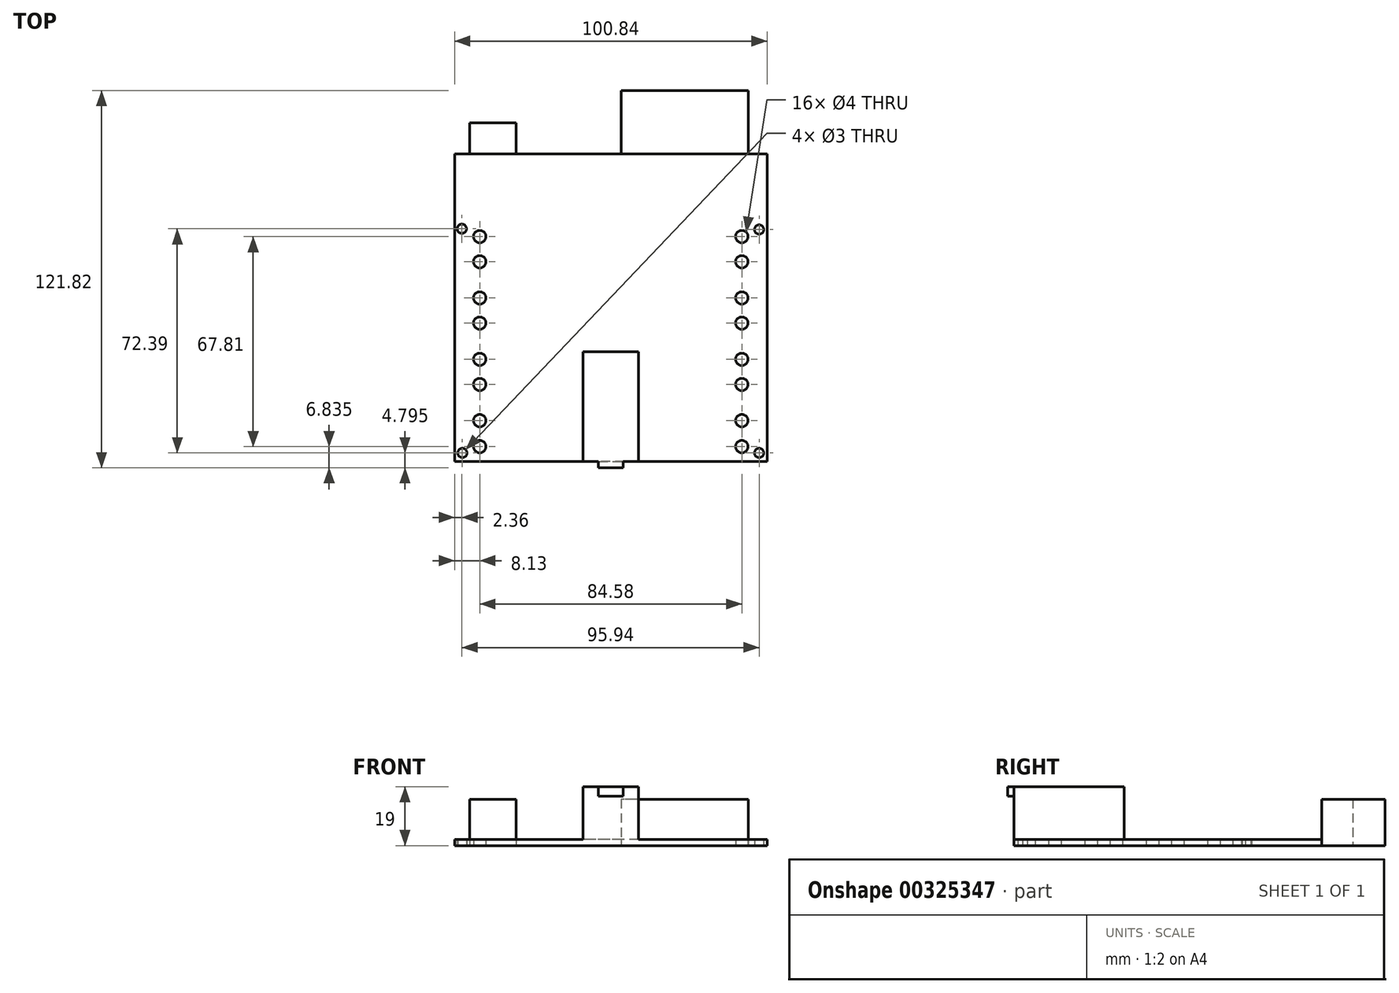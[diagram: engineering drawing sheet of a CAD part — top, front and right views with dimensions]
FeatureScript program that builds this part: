
annotation { "Feature Type Name" : "Feature", "Feature Type Description" : "" }
export const myFeature = defineFeature(function(context is Context, id is Id, definition is map)
    precondition{}
    {
        {
            var Q0;
            Q0=qCreatedBy(makeId("Top.planeOp"),FACE);
            var sketch = newSketch(context, id + "F0", { "sketchPlane" : qUnion([Q0])});
            skLineSegment(sketch, "E0.bottom", {"start": v(50.42, -49.66) * mm, "end": v(-50.42, -49.66) * mm});
            skLineSegment(sketch, "E0.top", {"start": v(50.42, 49.66) * mm, "end": v(-50.42, 49.66) * mm});
            skLineSegment(sketch, "E0.left", {"start": v(50.42, -49.66) * mm, "end": v(50.42, 49.66) * mm});
            skLineSegment(sketch, "E0.right", {"start": v(-50.42, -49.66) * mm, "end": v(-50.42, 49.66) * mm});
            skPoint(sketch, "E0.middle", {"position": v(0, 0) * mm});
            skCircle(sketch, "E1", {"center": v(-48.06, 25.53) * mm, "radius": 1.5 * mm});
            skCircle(sketch, "E2", {"center": v(47.88, -46.86) * mm, "radius": 1.5 * mm});
            skCircle(sketch, "E3", {"center": v(47.88, 25.28) * mm, "radius": 1.5 * mm});
            skCircle(sketch, "E4", {"center": v(-47.88, -46.87) * mm, "radius": 1.5 * mm});
            skCircle(sketch, "E5", {"center": v(-42.29, -44.83) * mm, "radius": 2 * mm});
            skCircle(sketch, "E6", {"center": v(-42.29, -36.45) * mm, "radius": 2 * mm});
            skCircle(sketch, "E7", {"center": v(-42.29, -24.77) * mm, "radius": 2 * mm});
            skCircle(sketch, "E8", {"center": v(-42.29, -16.64) * mm, "radius": 2 * mm});
            skCircle(sketch, "E9", {"center": v(-42.29, -4.96) * mm, "radius": 2 * mm});
            skCircle(sketch, "E10", {"center": v(-42.29, 3.17) * mm, "radius": 2 * mm});
            skCircle(sketch, "E11", {"center": v(-42.29, 14.85) * mm, "radius": 2 * mm});
            skCircle(sketch, "E12", {"center": v(-42.29, 22.98) * mm, "radius": 2 * mm});
            skCircle(sketch, "E13", {"center": v(42.3, -44.83) * mm, "radius": 2 * mm});
            skCircle(sketch, "E14", {"center": v(42.3, -36.45) * mm, "radius": 2 * mm});
            skCircle(sketch, "E15", {"center": v(42.29, -24.77) * mm, "radius": 2 * mm});
            skCircle(sketch, "E16", {"center": v(42.29, -16.64) * mm, "radius": 2 * mm});
            skCircle(sketch, "E17", {"center": v(42.29, -4.96) * mm, "radius": 2 * mm});
            skCircle(sketch, "E18", {"center": v(42.29, 3.17) * mm, "radius": 2 * mm});
            skCircle(sketch, "E19", {"center": v(42.29, 14.85) * mm, "radius": 2 * mm});
            skCircle(sketch, "E20", {"center": v(42.29, 22.98) * mm, "radius": 2 * mm});
            skSolve(sketch);
        }
        {
            var Q0;
            Q0=qSketchRegion(id+"F0",true);
            extrude(context, id + "F1", {"entities" : qUnion([Q0]), "depth" : 2 * mm});
        }
        {
            var Q0;
            Q0=makeQuery(id+"F1.opExtrude","CAP_FACE",FACE,{"disambiguationData":[OSD([sQuery(id+"F0.wireOp",EDGE,"E0.bottom"),sQuery(id+"F0.wireOp",EDGE,"E0.top"),sQuery(id+"F0.wireOp",EDGE,"E0.left"),sQuery(id+"F0.wireOp",EDGE,"E0.right"),sQuery(id+"F0.wireOp",EDGE,"E1"),sQuery(id+"F0.wireOp",EDGE,"E2"),sQuery(id+"F0.wireOp",EDGE,"E3"),sQuery(id+"F0.wireOp",EDGE,"E4")])],"isStart":false});
            cPlane(context, id + "F2", {"entities" : qUnion([Q0]), "cplaneType" : CPlaneType.OFFSET, "offset" : 0 * mm, "width" : 150 * mm, "height" : 150 * mm});
        }
        {
            var Q0;
            Q0=qCreatedBy(id+"F2.planeOp",FACE);
            var sketch = newSketch(context, id + "F3", { "sketchPlane" : qUnion([Q0])});
            skLineSegment(sketch, "E21.0", {"start": v(-50.42, -49.66) * mm, "end": v(-50.42, 49.66) * mm, "construction": true});
            skLineSegment(sketch, "E22.0", {"start": v(50.42, 49.66) * mm, "end": v(-50.42, 49.66) * mm, "construction": true});
            skLineSegment(sketch, "E23.0", {"start": v(50.42, -49.66) * mm, "end": v(50.42, 49.66) * mm, "construction": true});
            skLineSegment(sketch, "E24.0", {"start": v(50.42, -49.66) * mm, "end": v(-50.42, -49.66) * mm, "construction": true});
            skLineSegment(sketch, "E25.bottom", {"start": v(-45.6, 49.66) * mm, "end": v(-30.6, 49.66) * mm});
            skLineSegment(sketch, "E25.top", {"start": v(-45.6, 59.66) * mm, "end": v(-30.6, 59.66) * mm});
            skLineSegment(sketch, "E25.left", {"start": v(-45.6, 49.66) * mm, "end": v(-45.6, 59.66) * mm});
            skLineSegment(sketch, "E25.right", {"start": v(-30.6, 49.66) * mm, "end": v(-30.6, 59.66) * mm});
            skLineSegment(sketch, "E26.bottom", {"start": v(44.42, 49.66) * mm, "end": v(3.42, 49.66) * mm});
            skLineSegment(sketch, "E26.top", {"start": v(44.42, 70.16) * mm, "end": v(3.42, 70.16) * mm});
            skLineSegment(sketch, "E26.left", {"start": v(44.42, 49.66) * mm, "end": v(44.42, 70.16) * mm});
            skLineSegment(sketch, "E26.right", {"start": v(3.42, 49.66) * mm, "end": v(3.42, 70.16) * mm});
            skSolve(sketch);
        }
        {
            var Q0;
            Q0 = qSketchRegion(id + "F3", true);
            extrude(context, id + "F4", {"entities" : qUnion([Q0]), "operationType" : NewBodyOperationType.ADD, "depth" : 13 * mm, "hasSecondDirection" : true, "secondDirectionOppositeDirection" : true, "secondDirectionDepth" : 2 * mm});
        }
        {
            var Q0;
            Q0=qCreatedBy(id+"F2.planeOp",FACE);
            var sketch = newSketch(context, id + "F5", { "sketchPlane" : qUnion([Q0])});
            skLineSegment(sketch, "E27.0", {"start": v(50.42, -49.66) * mm, "end": v(-50.42, -49.66) * mm, "construction": true});
            skLineSegment(sketch, "E28.0", {"start": v(-50.42, -49.66) * mm, "end": v(-50.42, 49.66) * mm, "construction": true});
            skLineSegment(sketch, "E29.0", {"start": v(50.42, -49.66) * mm, "end": v(50.42, 49.66) * mm, "construction": true});
            skLineSegment(sketch, "E30.bottom", {"start": v(9, -49.66) * mm, "end": v(-9, -49.66) * mm});
            skLineSegment(sketch, "E30.top", {"start": v(9, -14.15) * mm, "end": v(-9, -14.16) * mm});
            skLineSegment(sketch, "E30.left", {"start": v(9, -49.66) * mm, "end": v(9, -14.15) * mm});
            skLineSegment(sketch, "E30.right", {"start": v(-9, -49.66) * mm, "end": v(-9, -14.16) * mm});
            skLineSegment(sketch, "E31", {"start": v(0, 0) * mm, "end": v(0, -49.66) * mm, "construction": true});
            skSolve(sketch);
        }
        {
            var Q0;
            Q0 = qSketchRegion(id + "F5", true);
            extrude(context, id + "F6", {"entities" : qUnion([Q0]), "operationType" : NewBodyOperationType.ADD, "depth" : 17 * mm});
        }
        {
            var Q0;
            Q0=makeQuery(id+"F6.boolean.opBoolean","MERGE",FACE,{"derivedFrom":[makeQuery(id+"F1.opExtrude","SWEPT_FACE",FACE,{"disambiguationData":[OSD([sQuery(id+"F0.wireOp",EDGE,"E0.bottom")])]}),makeQuery(id+"F6.opExtrude","SWEPT_FACE",FACE,{"disambiguationData":[OSD([sQuery(id+"F5.wireOp",EDGE,"E30.bottom")])]})]});
            cPlane(context, id + "F7", {"entities" : qUnion([Q0]), "cplaneType" : CPlaneType.OFFSET, "offset" : 0 * mm, "width" : 150 * mm, "height" : 150 * mm});
        }
        {
            var Q0;
            Q0=qCreatedBy(id+"F7.planeOp",FACE);
            var sketch = newSketch(context, id + "F8", { "sketchPlane" : qUnion([Q0])});
            skLineSegment(sketch, "E32.0", {"start": v(9, 19) * mm, "end": v(-9, 19) * mm, "construction": true});
            skLineSegment(sketch, "E33.0", {"start": v(50.42, 0) * mm, "end": v(-50.42, 0) * mm, "construction": true});
            skLineSegment(sketch, "E34", {"start": v(0, 19) * mm, "end": v(0, 0) * mm, "construction": true});
            skLineSegment(sketch, "E35.bottom", {"start": v(-4, 19) * mm, "end": v(4, 19) * mm});
            skLineSegment(sketch, "E35.top", {"start": v(-4, 16) * mm, "end": v(4, 16) * mm});
            skLineSegment(sketch, "E35.left", {"start": v(-4, 19) * mm, "end": v(-4, 16) * mm});
            skLineSegment(sketch, "E35.right", {"start": v(4, 19) * mm, "end": v(4, 16) * mm});
            skSolve(sketch);
        }
        {
            var Q0;
            Q0 = qSketchRegion(id + "F8", true);
            extrude(context, id + "F9", {"entities" : qUnion([Q0]), "operationType" : NewBodyOperationType.ADD, "depth" : 2 * mm});
        }
    });
